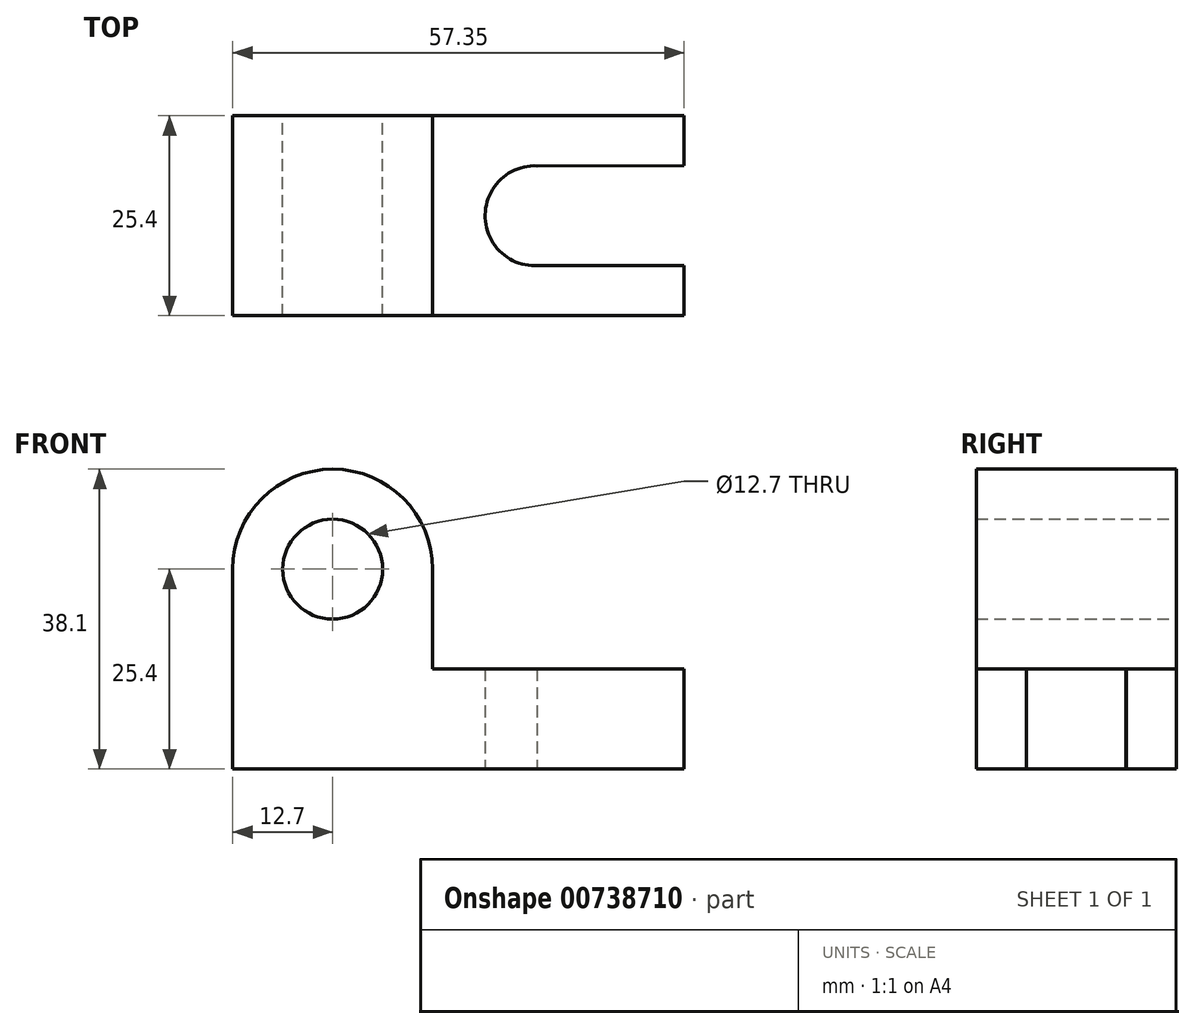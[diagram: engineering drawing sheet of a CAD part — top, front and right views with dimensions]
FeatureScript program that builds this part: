
annotation { "Feature Type Name" : "Feature", "Feature Type Description" : "" }
export const myFeature = defineFeature(function(context is Context, id is Id, definition is map)
    precondition{}
    {
        {
            var Q0;
            Q0=qCreatedBy(makeId("Front.planeOp"),FACE);
            var sketch = newSketch(context, id + "F0", { "sketchPlane" : qUnion([Q0])});
            skLineSegment(sketch, "E0", {"start": v(0, 38.1) * mm, "end": v(0, 0) * mm});
            skLineSegment(sketch, "E1", {"start": v(0, 0) * mm, "end": v(69.85, 0) * mm});
            skLineSegment(sketch, "E2", {"start": v(69.85, 0) * mm, "end": v(69.85, 12.7) * mm});
            skLineSegment(sketch, "E3", {"start": v(69.85, 12.7) * mm, "end": v(25.4, 12.7) * mm});
            skLineSegment(sketch, "E4", {"start": v(25.4, 12.7) * mm, "end": v(25.4, 38.1) * mm});
            skLineSegment(sketch, "E5", {"start": v(25.4, 38.1) * mm, "end": v(0, 38.1) * mm});
            skSolve(sketch);
        }
        {
            var Q0;
            Q0 = qSketchRegion(id + "F0", true);
            extrude(context, id + "F1", {"entities" : qUnion([Q0]), "depth" : 25.4 * mm, "offsetDistance" : 25.4 * mm});
        }
        {
            var Q0;
            Q0=qCreatedBy(makeId("Front.planeOp"),FACE);
            var sketch = newSketch(context, id + "F2", { "sketchPlane" : qUnion([Q0])});
            skLineSegment(sketch, "E6", {"start": v(0, 25.4) * mm, "end": v(25.4, 25.4) * mm});
            skCircle(sketch, "E7", {"center": v(12.7, 25.4) * mm, "radius": 6.35 * mm});
            skSolve(sketch);
        }
        {
            var Q0;
            Q0 = qSketchRegion(id + "F2", true);
            extrude(context, id + "F3", {"entities" : qUnion([Q0]), "operationType" : NewBodyOperationType.REMOVE, "endBound" : BoundingType.THROUGH_ALL, "depth" : 25.4 * mm, "offsetDistance" : 25.4 * mm});
        }
        {
            var Q0;
            Q0=qCreatedBy(makeId("Top.planeOp"),FACE);
            var sketch = newSketch(context, id + "F4", { "sketchPlane" : qUnion([Q0])});
            skLineSegment(sketch, "E8", {"start": v(25.71, -12.7) * mm, "end": v(70.16, -12.7) * mm});
            skCircle(sketch, "E9", {"center": v(38.41, -12.7) * mm, "radius": 6.35 * mm});
            skCircle(sketch, "E10", {"center": v(57.46, -12.7) * mm, "radius": 6.35 * mm});
            skLineSegment(sketch, "E11", {"start": v(38.15, -6.36) * mm, "end": v(57.46, -6.35) * mm});
            skLineSegment(sketch, "E12", {"start": v(38.41, -19.05) * mm, "end": v(57.46, -19.05) * mm});
            skLineSegment(sketch, "E13", {"start": v(57.46, -19.05) * mm, "end": v(104.84, -14.86) * mm});
            skSolve(sketch);
        }
        {
            var Q0;
            Q0 = qSketchRegion(id + "F4", true);
            extrude(context, id + "F5", {"entities" : qUnion([Q0]), "operationType" : NewBodyOperationType.REMOVE, "endBound" : BoundingType.THROUGH_ALL, "depth" : 25.4 * mm, "offsetDistance" : 25.4 * mm});
        }
        {
            var Q0;
            Q0=qCreatedBy(makeId("Top.planeOp"),FACE);
            var sketch = newSketch(context, id + "F6", { "sketchPlane" : qUnion([Q0])});
            skArc(sketch, "E14", {"start": v(57.15, -25.4) * mm, "mid": v(69.85, -12.7) * mm, "end": v(57.15, 0) * mm});
            skLineSegment(sketch, "E15", {"start": v(69.85, -12.7) * mm, "end": v(69.85, -25.3) * mm});
            skLineSegment(sketch, "E16", {"start": v(69.85, -25.3) * mm, "end": v(57.15, -25.4) * mm});
            skArc(sketch, "E17", {"start": v(57.15, -25.4) * mm, "mid": v(66.1, -21.65) * mm, "end": v(69.85, -12.7) * mm});
            skLineSegment(sketch, "E18", {"start": v(57.15, 0) * mm, "end": v(70.14, 0) * mm});
            skLineSegment(sketch, "E19", {"start": v(70.14, 0) * mm, "end": v(69.85, -25.3) * mm});
            skSolve(sketch);
        }
        {
            var Q0;
            Q0 = qSketchRegion(id + "F6", true);
            extrude(context, id + "F7", {"entities" : qUnion([Q0]), "operationType" : NewBodyOperationType.REMOVE, "endBound" : BoundingType.THROUGH_ALL, "depth" : 25.4 * mm, "offsetDistance" : 25.4 * mm});
        }
        {
            var Q0;
            Q0=qCreatedBy(makeId("Top.planeOp"),FACE);
            var sketch = newSketch(context, id + "F8", { "sketchPlane" : qUnion([Q0])});
            skSolve(sketch);
        }
        {
            var Q0;
            Q0 = qSketchRegion(id + "F8", true);
            var Q1;
            {var subQ0=sQuery(id+"F0.wireOp",EDGE,"E1");var subQ1=sQuery(id+"F0.wireOp",EDGE,"E2");var subQ2=sQuery(id+"F0.wireOp",EDGE,"E3");Q1=makeQuery(id+"F7.boolean.opBoolean","SPLIT",FACE,{"disambiguationData":[TD([makeQuery(id+"F1.opExtrude","SWEPT_FACE",FACE,{"disambiguationData":[OSD([subQ1])]})])],"derivedFrom":makeQuery(id+"F1.opExtrude","CAP_FACE",FACE,{"disambiguationData":[OSD([sQuery(id+"F0.wireOp",EDGE,"E0"),subQ0,subQ1,subQ2,sQuery(id+"F0.wireOp",EDGE,"E4"),sQuery(id+"F0.wireOp",EDGE,"E5")])],"isStart":false})});}
            extrude(context, id + "F9", {"entities" : qUnion([Q0, Q1]), "operationType" : NewBodyOperationType.REMOVE, "oppositeDirection" : true, "depth" : 25.4 * mm, "offsetDistance" : 25.4 * mm});
        }
        {
            var Q0;
            Q0 = qSketchRegion(id + "F6", true);
            extrude(context, id + "F10", {"entities" : qUnion([Q0]), "operationType" : NewBodyOperationType.REMOVE, "oppositeDirection" : true, "depth" : 25.4 * mm, "offsetDistance" : 25.4 * mm});
        }
        {
            var Q0;
            Q0=qCreatedBy(makeId("Front.planeOp"),FACE);
            var sketch = newSketch(context, id + "F11", { "sketchPlane" : qUnion([Q0])});
            skArc(sketch, "E20", {"start": v(25.4, 25.4) * mm, "mid": v(12.7, 38.1) * mm, "end": v(0, 25.4) * mm});
            skLineSegment(sketch, "E21", {"start": v(0, 25.4) * mm, "end": v(0, 38.1) * mm});
            skLineSegment(sketch, "E22", {"start": v(0, 38.1) * mm, "end": v(25.4, 38.1) * mm});
            skLineSegment(sketch, "E23", {"start": v(25.4, 38.1) * mm, "end": v(25.4, 25.4) * mm});
            skSolve(sketch);
        }
        {
            var Q0;
            Q0 = qSketchRegion(id + "F11", true);
            extrude(context, id + "F12", {"entities" : qUnion([Q0]), "operationType" : NewBodyOperationType.REMOVE, "depth" : 25.4 * mm, "offsetDistance" : 25.4 * mm});
        }
    });
